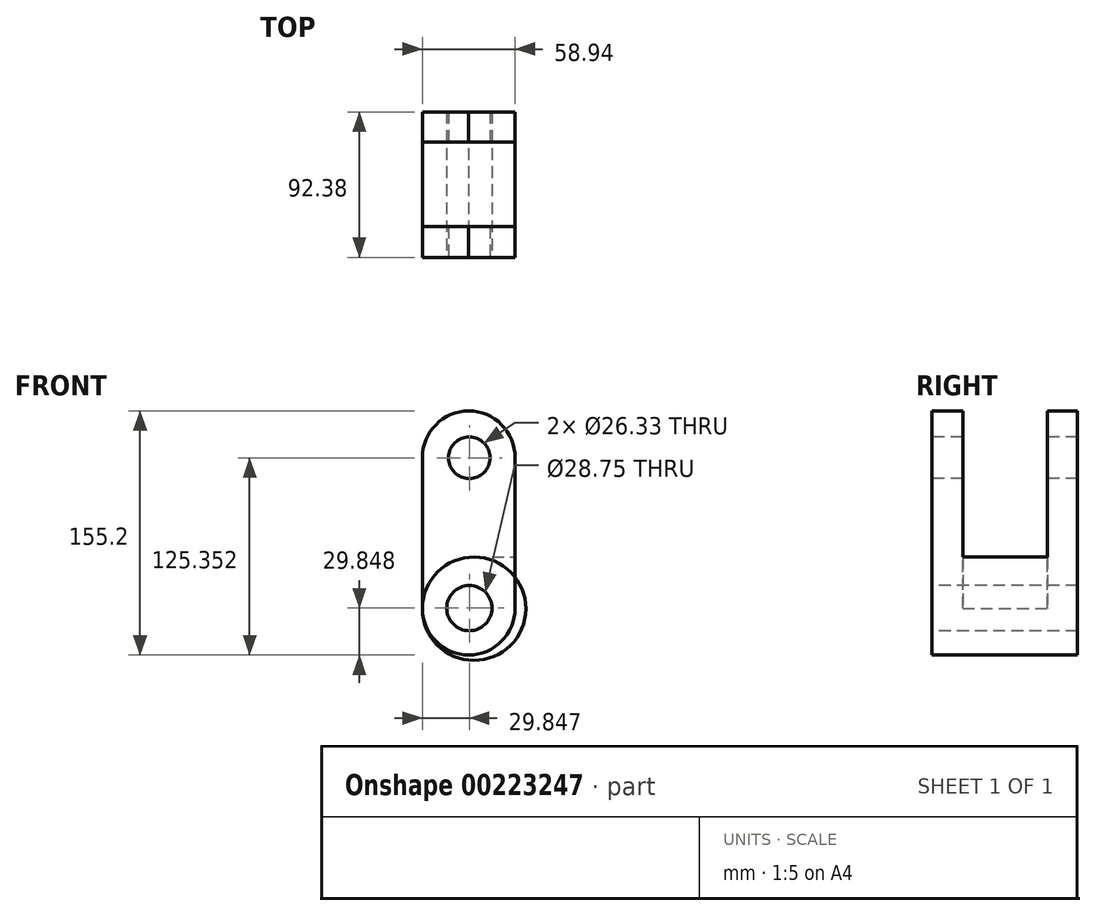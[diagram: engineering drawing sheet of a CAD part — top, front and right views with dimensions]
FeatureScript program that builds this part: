
annotation { "Feature Type Name" : "Feature", "Feature Type Description" : "" }
export const myFeature = defineFeature(function(context is Context, id is Id, definition is map)
    precondition{}
    {
        {
            var Q0;
            Q0=qCreatedBy(makeId("Front.planeOp"),FACE);
            var sketch = newSketch(context, id + "F0", { "sketchPlane" : qUnion([Q0])});
            skLineSegment(sketch, "E0.bottom", {"start": v(29.47, -77.6) * mm, "end": v(-29.47, -77.6) * mm});
            skLineSegment(sketch, "E0.top", {"start": v(29.47, 77.6) * mm, "end": v(-29.47, 77.6) * mm});
            skLineSegment(sketch, "E0.left", {"start": v(29.47, -77.6) * mm, "end": v(29.47, 77.6) * mm});
            skLineSegment(sketch, "E0.right", {"start": v(-29.47, -77.6) * mm, "end": v(-29.47, 77.6) * mm});
            skPoint(sketch, "E0.middle", {"position": v(0, 0) * mm});
            skSolve(sketch);
        }
        {
            var Q0;
            Q0=makeQuery(id+"F0.imprint","IMPRINT",FACE,{"disambiguationData":[TD([[makeQuery(id+"F0.imprint","IMPRINT",EDGE,{"derivedFrom":sQuery(id+"F0.wireOp",EDGE,"E0.bottom")}),-1.0]])]});
            extrude(context, id + "F4", {"entities" : qUnion([Q0]), "endBound" : BoundingType.SYMMETRIC, "depth" : 92.38 * mm});
        }
        {
            var Q0;
            Q0=makeQuery(id+"F4.opExtrude","SWEPT_FACE",FACE,{"disambiguationData":[OSD([sQuery(id+"F0.wireOp",EDGE,"E0.left")])]});
            var sketch = newSketch(context, id + "F5", { "sketchPlane" : qUnion([Q0])});
            skLineSegment(sketch, "E1.bottom", {"start": v(-26.7, 77.6) * mm, "end": v(27.13, 77.6) * mm});
            skLineSegment(sketch, "E1.top", {"start": v(-26.7, -15.26) * mm, "end": v(27.13, -15.26) * mm});
            skLineSegment(sketch, "E1.left", {"start": v(-26.7, 77.6) * mm, "end": v(-26.7, -15.26) * mm});
            skLineSegment(sketch, "E1.right", {"start": v(27.13, 77.6) * mm, "end": v(27.13, -15.26) * mm});
            skSolve(sketch);
        }
        {
            var Q0;
            Q0=makeQuery(id+"F5.imprint","IMPRINT",FACE,{"disambiguationData":[TD([[makeQuery(id+"F5.imprint","IMPRINT",EDGE,{"derivedFrom":sQuery(id+"F5.wireOp",EDGE,"E1.bottom")}),-1.0]])]});
            extrude(context, id + "F1", {"entities" : qUnion([Q0]), "operationType" : NewBodyOperationType.REMOVE, "endBound" : BoundingType.THROUGH_ALL, "oppositeDirection" : true, "depth" : 25.4 * mm});
        }
        {
            var Q0;
            {var subQ0=sQuery(id+"F0.wireOp",EDGE,"E0.left");var subQ1=sQuery(id+"F0.wireOp",EDGE,"E0.top");Q0=makeQuery(id+"F1.boolean.opBoolean","SPLIT",EDGE,{"disambiguationData":[TD([makeQuery(id+"F1.opExtrude","SWEPT_FACE",FACE,{"disambiguationData":[OSD([sQuery(id+"F5.wireOp",EDGE,"E1.right")])]})])],"derivedFrom":makeQuery(id+"F4.opExtrude","SWEPT_EDGE",EDGE,{"disambiguationData":[OSD([subQ1,subQ0])]})});}
            var Q1;
            {var subQ0=sQuery(id+"F0.wireOp",EDGE,"E0.right");var subQ1=sQuery(id+"F0.wireOp",EDGE,"E0.top");Q1=makeQuery(id+"F1.boolean.opBoolean","SPLIT",EDGE,{"disambiguationData":[TD([makeQuery(id+"F1.opExtrude","SWEPT_FACE",FACE,{"disambiguationData":[OSD([sQuery(id+"F5.wireOp",EDGE,"E1.right")])]})])],"derivedFrom":makeQuery(id+"F4.opExtrude","SWEPT_EDGE",EDGE,{"disambiguationData":[OSD([subQ1,subQ0])]})});}
            var Q2;
            {var subQ0=sQuery(id+"F0.wireOp",EDGE,"E0.left");var subQ1=sQuery(id+"F0.wireOp",EDGE,"E0.top");Q2=makeQuery(id+"F1.boolean.opBoolean","SPLIT",EDGE,{"disambiguationData":[TD([makeQuery(id+"F1.opExtrude","SWEPT_FACE",FACE,{"disambiguationData":[OSD([sQuery(id+"F5.wireOp",EDGE,"E1.left")])]})])],"derivedFrom":makeQuery(id+"F4.opExtrude","SWEPT_EDGE",EDGE,{"disambiguationData":[OSD([subQ1,subQ0])]})});}
            var Q3;
            {var subQ0=sQuery(id+"F0.wireOp",EDGE,"E0.right");var subQ1=sQuery(id+"F0.wireOp",EDGE,"E0.top");Q3=makeQuery(id+"F1.boolean.opBoolean","SPLIT",EDGE,{"disambiguationData":[TD([makeQuery(id+"F1.opExtrude","SWEPT_FACE",FACE,{"disambiguationData":[OSD([sQuery(id+"F5.wireOp",EDGE,"E1.left")])]})])],"derivedFrom":makeQuery(id+"F4.opExtrude","SWEPT_EDGE",EDGE,{"disambiguationData":[OSD([subQ1,subQ0])]})});}
            var Q4;
            Q4=makeQuery(id+"F4.opExtrude","SWEPT_EDGE",EDGE,{"disambiguationData":[OSD([sQuery(id+"F0.wireOp",EDGE,"E0.bottom"),sQuery(id+"F0.wireOp",EDGE,"E0.left")])]});
            var Q5;
            Q5=makeQuery(id+"F4.opExtrude","SWEPT_EDGE",EDGE,{"disambiguationData":[OSD([sQuery(id+"F0.wireOp",EDGE,"E0.bottom"),sQuery(id+"F0.wireOp",EDGE,"E0.right")])]});
            fillet(context, id + "F2", {"entities" : qUnion([Q0, Q1, Q2, Q3, Q4, Q5]), "radius" : 29.85 * mm, "tangentPropagation" : true, "allowEdgeOverflow" : false});
        }
        {
            var Q0;
            Q0=makeQuery(id+"F1.boolean.opBoolean","COPY",EDGE,{"derivedFrom":makeQuery(id+"F1.opExtrude","CAP_EDGE",EDGE,{"disambiguationData":[OSD([sQuery(id+"F5.wireOp",EDGE,"E1.top")])],"isStart":true})});
            var Q1;
            Q1=makeQuery(id+"F1.boolean.opBoolean","INTERSECT",EDGE,{"derivedFrom":[makeQuery(id+"F4.opExtrude","SWEPT_FACE",FACE,{"disambiguationData":[OSD([sQuery(id+"F0.wireOp",EDGE,"E0.right")])]}),makeQuery(id+"F1.opExtrude","SWEPT_FACE",FACE,{"disambiguationData":[OSD([sQuery(id+"F5.wireOp",EDGE,"E1.top")])]})]});
            fillet(context, id + "F3", {"entities" : qUnion([Q0, Q1]), "radius" : 32.85 * mm, "tangentPropagation" : true, "allowEdgeOverflow" : false});
        }
        {
            var Q0;
            Q0=makeQuery(id+"F4.opExtrude","CAP_FACE",FACE,{"disambiguationData":[OSD([sQuery(id+"F0.wireOp",EDGE,"E0.bottom"),sQuery(id+"F0.wireOp",EDGE,"E0.top"),sQuery(id+"F0.wireOp",EDGE,"E0.left"),sQuery(id+"F0.wireOp",EDGE,"E0.right")])],"isStart":false});
            var sketch = newSketch(context, id + "F6", { "sketchPlane" : qUnion([Q0])});
            skCircle(sketch, "E2", {"center": v(0.38, 47.75) * mm, "radius": 13.16 * mm});
            skCircle(sketch, "E3", {"center": v(0.38, -47.75) * mm, "radius": 14.38 * mm});
            skSolve(sketch);
        }
        {
            var Q0;
            Q0=makeQuery(id+"F6.imprint","IMPRINT",FACE,{"disambiguationData":[TD([[makeQuery(id+"F6.imprint","IMPRINT",EDGE,{"derivedFrom":sQuery(id+"F6.wireOp",EDGE,"E2")}),1.0]])]});
            var Q1;
            Q1=makeQuery(id+"F6.imprint","IMPRINT",FACE,{"disambiguationData":[TD([[makeQuery(id+"F6.imprint","IMPRINT",EDGE,{"derivedFrom":sQuery(id+"F6.wireOp",EDGE,"E3")}),1.0]])]});
            extrude(context, id + "F7", {"entities" : qUnion([Q0, Q1]), "operationType" : NewBodyOperationType.REMOVE, "endBound" : BoundingType.THROUGH_ALL, "oppositeDirection" : true, "depth" : 25.4 * mm});
        }
    });
